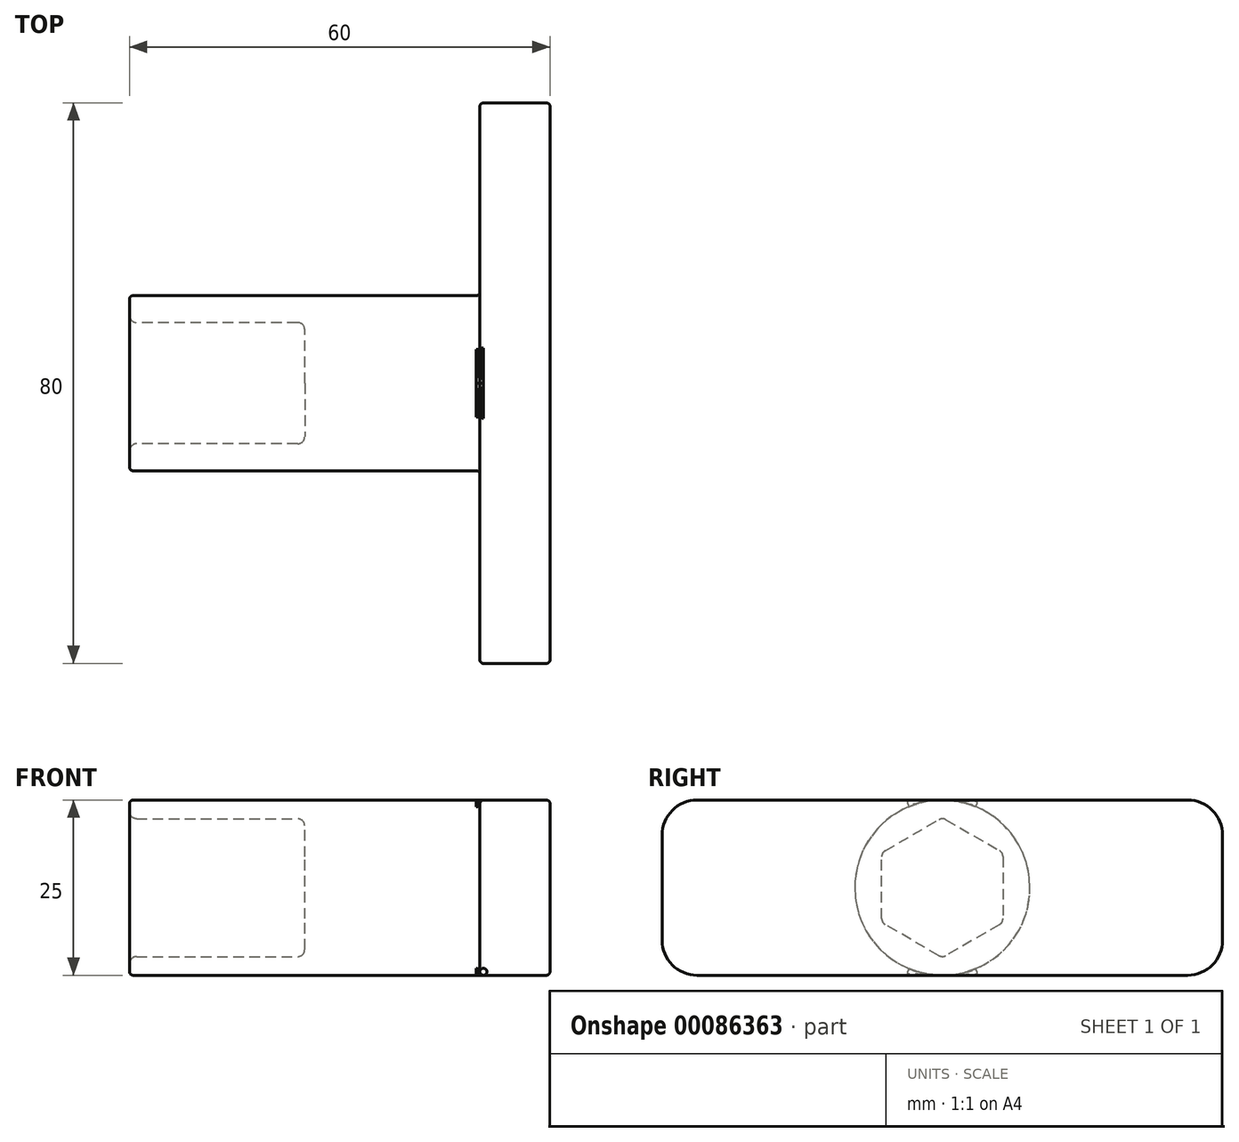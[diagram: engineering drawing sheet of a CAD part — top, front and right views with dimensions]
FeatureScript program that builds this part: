
annotation { "Feature Type Name" : "Feature", "Feature Type Description" : "" }
export const myFeature = defineFeature(function(context is Context, id is Id, definition is map)
    precondition{}
    {
        {
            var Q0;
            Q0=qCreatedBy(makeId("Right.planeOp"),FACE);
            var sketch = newSketch(context, id + "F0", { "sketchPlane" : qUnion([Q0])});
            skCircle(sketch, "E0", {"center": v(0, 0) * mm, "radius": 12.5 * mm});
            skCircle(sketch, "E1.cCircle", {"center": v(0, 0) * mm, "radius": 8.65 * mm, "construction": true});
            skLineSegment(sketch, "E1.0", {"start": v(-8.65, 5) * mm, "end": v(0, 9.99) * mm});
            skLineSegment(sketch, "E1.1", {"start": v(0, 9.99) * mm, "end": v(8.65, 5) * mm});
            skLineSegment(sketch, "E1.2", {"start": v(8.65, 5) * mm, "end": v(8.65, -5) * mm});
            skLineSegment(sketch, "E1.3", {"start": v(8.65, -5) * mm, "end": v(0, -9.99) * mm});
            skLineSegment(sketch, "E1.4", {"start": v(0, -9.99) * mm, "end": v(-8.65, -5) * mm});
            skLineSegment(sketch, "E1.5", {"start": v(-8.65, -5) * mm, "end": v(-8.65, 5) * mm});
            skPoint(sketch, "E1.0.midPoint", {"position": v(-4.32, 7.5) * mm});
            skSolve(sketch);
        }
        {
            var Q0;
            Q0 = qSketchRegion(id + "F0", true);
            extrude(context, id + "F1", {"entities" : qUnion([Q0]), "depth" : 25 * mm, "offsetDistance" : 25 * mm});
        }
        {
            var Q0;
            Q0=makeQuery(id+"F1.opExtrude","CAP_FACE",FACE,{"disambiguationData":[OSD([sQuery(id+"F0.wireOp",EDGE,"E0"),sQuery(id+"F0.wireOp",EDGE,"E1.0"),sQuery(id+"F0.wireOp",EDGE,"E1.1"),sQuery(id+"F0.wireOp",EDGE,"E1.2"),sQuery(id+"F0.wireOp",EDGE,"E1.3"),sQuery(id+"F0.wireOp",EDGE,"E1.4"),sQuery(id+"F0.wireOp",EDGE,"E1.5")])],"isStart":false});
            extrude(context, id + "F2", {"entities" : qUnion([Q0]), "operationType" : NewBodyOperationType.ADD, "depth" : 25 * mm, "offsetDistance" : 25 * mm});
        }
        {
            var Q0;
            Q0=makeQuery(id+"F2.opExtrude","CAP_FACE",FACE,{"disambiguationData":[OSD([sQuery(id+"F0.wireOp",EDGE,"E0"),sQuery(id+"F0.wireOp",EDGE,"E1.0"),sQuery(id+"F0.wireOp",EDGE,"E1.1"),sQuery(id+"F0.wireOp",EDGE,"E1.2"),sQuery(id+"F0.wireOp",EDGE,"E1.3"),sQuery(id+"F0.wireOp",EDGE,"E1.4"),sQuery(id+"F0.wireOp",EDGE,"E1.5")])],"isStart":false});
            var sketch = newSketch(context, id + "F3", { "sketchPlane" : qUnion([Q0])});
            skLineSegment(sketch, "E2", {"start": v(0, 9.99) * mm, "end": v(0, -9.99) * mm});
            skLineSegment(sketch, "E3.bottom", {"start": v(40, 12.5) * mm, "end": v(-40, 12.5) * mm});
            skLineSegment(sketch, "E3.top", {"start": v(40, -12.5) * mm, "end": v(-40, -12.5) * mm});
            skLineSegment(sketch, "E3.left", {"start": v(40, 12.5) * mm, "end": v(40, -12.5) * mm});
            skLineSegment(sketch, "E3.right", {"start": v(-40, 12.5) * mm, "end": v(-40, -12.5) * mm});
            skPoint(sketch, "E3.middle", {"position": v(0, 0) * mm});
            skSolve(sketch);
        }
        {
            var Q0;
            Q0 = qSketchRegion(id + "F3", true);
            extrude(context, id + "F4", {"entities" : qUnion([Q0]), "operationType" : NewBodyOperationType.ADD, "depth" : 10 * mm, "offsetDistance" : 25 * mm});
        }
        {
            var Q0;
            Q0=makeQuery(id+"F4.opExtrude","SWEPT_EDGE",EDGE,{"disambiguationData":[OSD([sQuery(id+"F3.wireOp",EDGE,"E3.bottom"),sQuery(id+"F3.wireOp",EDGE,"E3.right")])]});
            var Q1;
            Q1=makeQuery(id+"F4.opExtrude","SWEPT_EDGE",EDGE,{"disambiguationData":[OSD([sQuery(id+"F3.wireOp",EDGE,"E3.top"),sQuery(id+"F3.wireOp",EDGE,"E3.right")])]});
            var Q2;
            Q2=makeQuery(id+"F4.opExtrude","SWEPT_EDGE",EDGE,{"disambiguationData":[OSD([sQuery(id+"F3.wireOp",EDGE,"E3.bottom"),sQuery(id+"F3.wireOp",EDGE,"E3.left")])]});
            var Q3;
            Q3=makeQuery(id+"F4.opExtrude","SWEPT_EDGE",EDGE,{"disambiguationData":[OSD([sQuery(id+"F3.wireOp",EDGE,"E3.top"),sQuery(id+"F3.wireOp",EDGE,"E3.left")])]});
            fillet(context, id + "F5", {"entities" : qUnion([Q0, Q1, Q2, Q3]), "radius" : 5 * mm, "tangentPropagation" : true, "allowEdgeOverflow" : false});
        }
        {
            var Q0;
            Q0=makeQuery(id+"F4.opExtrude","CAP_FACE",FACE,{"disambiguationData":[OSD([sQuery(id+"F3.wireOp",EDGE,"E3.bottom"),sQuery(id+"F3.wireOp",EDGE,"E3.top"),sQuery(id+"F3.wireOp",EDGE,"E3.left"),sQuery(id+"F3.wireOp",EDGE,"E3.right")])],"isStart":false});
            var Q1;
            {var subQ0=sQuery(id+"F0.wireOp",EDGE,"E0");Q1=makeQuery(id+"F2.boolean.opBoolean","MERGE",FACE,{"derivedFrom":[makeQuery(id+"F1.opExtrude","SWEPT_FACE",FACE,{"disambiguationData":[OSD([subQ0])]}),makeQuery(id+"F2.opExtrude","SWEPT_FACE",FACE,{"disambiguationData":[OSD([subQ0])]})]});}
            var Q2;
            {var subQ0=sQuery(id+"F3.wireOp",EDGE,"E3.right");var subQ1=sQuery(id+"F3.wireOp",EDGE,"E3.top");var subQ2=sQuery(id+"F3.wireOp",EDGE,"E3.bottom");var subQ3=makeQuery(id+"F4.opExtrude","CAP_FACE",FACE,{"disambiguationData":[OSD([subQ2,subQ1,sQuery(id+"F3.wireOp",EDGE,"E3.left"),subQ0])],"isStart":true});Q2=makeQuery(id+"F5.opFillet","BLEND_EDGE",EDGE,{"blendedFrom":[makeQuery(id+"F4.opExtrude","SWEPT_EDGE",EDGE,{"disambiguationData":[OSD([subQ1,subQ0])]}),makeQuery(id+"F4.boolean.opBoolean","SPLIT",FACE,{"disambiguationData":[TD([makeQuery(id+"F4.opExtrude","SWEPT_FACE",FACE,{"disambiguationData":[OSD([subQ0])]})])],"derivedFrom":subQ3})],"blendedInto":[makeQuery(id+"F4.boolean.opBoolean","SPLIT",FACE,{"disambiguationData":[TD([makeQuery(id+"F4.opExtrude","SWEPT_FACE",FACE,{"disambiguationData":[OSD([subQ0])]})])],"derivedFrom":subQ3})]});}
            var Q3;
            {var subQ0=sQuery(id+"F3.wireOp",EDGE,"E3.top");var subQ1=sQuery(id+"F3.wireOp",EDGE,"E3.left");Q3=makeQuery(id+"F4.boolean.opBoolean","SPLIT",EDGE,{"disambiguationData":[TD([makeQuery(id+"F4.opExtrude","SWEPT_FACE",FACE,{"disambiguationData":[OSD([subQ1])]})])],"derivedFrom":makeQuery(id+"F4.opExtrude","CAP_EDGE",EDGE,{"disambiguationData":[OSD([subQ0])],"isStart":true})});}
            fillet(context, id + "F6", {"entities" : qUnion([Q0, Q1, Q2, Q3]), "radius" : .5 * mm, "tangentPropagation" : true, "allowEdgeOverflow" : false});
        }
        {
            var Q0;
            {var subQ4=sQuery(id+"F0.wireOp",EDGE,"E1.0");Q0=makeQuery(id+"F4.boolean.opBoolean","SPLIT",FACE,{"disambiguationData":[TD([makeQuery(id+"F1.opExtrude","SWEPT_FACE",FACE,{"disambiguationData":[OSD([subQ4])]})])],"derivedFrom":makeQuery(id+"F4.opExtrude","CAP_FACE",FACE,{"disambiguationData":[OSD([sQuery(id+"F3.wireOp",EDGE,"E3.bottom"),sQuery(id+"F3.wireOp",EDGE,"E3.top"),sQuery(id+"F3.wireOp",EDGE,"E3.left"),sQuery(id+"F3.wireOp",EDGE,"E3.right")])],"isStart":true})});}
            extrude(context, id + "F7", {"entities" : qUnion([Q0]), "operationType" : NewBodyOperationType.ADD, "depth" : 25 * mm, "offsetDistance" : 25 * mm});
        }
        {
            var Q0;
            {var subQ0=sQuery(id+"F0.wireOp",EDGE,"E1.4");var subQ1=sQuery(id+"F0.wireOp",EDGE,"E1.3");Q0=makeQuery(id+"F2.boolean.opBoolean","MERGE",EDGE,{"derivedFrom":[makeQuery(id+"F1.opExtrude","SWEPT_EDGE",EDGE,{"disambiguationData":[OSD([subQ1,subQ0])]}),makeQuery(id+"F2.opExtrude","SWEPT_EDGE",EDGE,{"disambiguationData":[OSD([subQ1,subQ0])]})]});}
            var Q1;
            {var subQ0=sQuery(id+"F0.wireOp",EDGE,"E1.3");var subQ1=sQuery(id+"F0.wireOp",EDGE,"E1.2");Q1=makeQuery(id+"F2.boolean.opBoolean","MERGE",EDGE,{"derivedFrom":[makeQuery(id+"F1.opExtrude","SWEPT_EDGE",EDGE,{"disambiguationData":[OSD([subQ1,subQ0])]}),makeQuery(id+"F2.opExtrude","SWEPT_EDGE",EDGE,{"disambiguationData":[OSD([subQ1,subQ0])]})]});}
            var Q2;
            {var subQ0=sQuery(id+"F0.wireOp",EDGE,"E1.5");var subQ1=sQuery(id+"F0.wireOp",EDGE,"E1.4");Q2=makeQuery(id+"F2.boolean.opBoolean","MERGE",EDGE,{"derivedFrom":[makeQuery(id+"F1.opExtrude","SWEPT_EDGE",EDGE,{"disambiguationData":[OSD([subQ1,subQ0])]}),makeQuery(id+"F2.opExtrude","SWEPT_EDGE",EDGE,{"disambiguationData":[OSD([subQ1,subQ0])]})]});}
            var Q3;
            {var subQ0=sQuery(id+"F0.wireOp",EDGE,"E1.5");var subQ1=sQuery(id+"F0.wireOp",EDGE,"E1.0");Q3=makeQuery(id+"F2.boolean.opBoolean","MERGE",EDGE,{"derivedFrom":[makeQuery(id+"F1.opExtrude","SWEPT_EDGE",EDGE,{"disambiguationData":[OSD([subQ1,subQ0])]}),makeQuery(id+"F2.opExtrude","SWEPT_EDGE",EDGE,{"disambiguationData":[OSD([subQ1,subQ0])]})]});}
            var Q4;
            {var subQ0=sQuery(id+"F0.wireOp",EDGE,"E1.1");var subQ1=sQuery(id+"F0.wireOp",EDGE,"E1.0");Q4=makeQuery(id+"F2.boolean.opBoolean","MERGE",EDGE,{"derivedFrom":[makeQuery(id+"F1.opExtrude","SWEPT_EDGE",EDGE,{"disambiguationData":[OSD([subQ1,subQ0])]}),makeQuery(id+"F2.opExtrude","SWEPT_EDGE",EDGE,{"disambiguationData":[OSD([subQ1,subQ0])]})]});}
            var Q5;
            {var subQ0=sQuery(id+"F0.wireOp",EDGE,"E1.2");var subQ1=sQuery(id+"F0.wireOp",EDGE,"E1.1");Q5=makeQuery(id+"F2.boolean.opBoolean","MERGE",EDGE,{"derivedFrom":[makeQuery(id+"F1.opExtrude","SWEPT_EDGE",EDGE,{"disambiguationData":[OSD([subQ1,subQ0])]}),makeQuery(id+"F2.opExtrude","SWEPT_EDGE",EDGE,{"disambiguationData":[OSD([subQ1,subQ0])]})]});}
            fillet(context, id + "F8", {"entities" : qUnion([Q0, Q1, Q2, Q3, Q4, Q5]), "radius" : 1 * mm, "tangentPropagation" : true, "allowEdgeOverflow" : false});
        }
        {
            var Q0;
            Q0=makeQuery(id+"F7.opExtrude","CAP_FACE",FACE,{"disambiguationData":[OSD([sQuery(id+"F3.wireOp",EDGE,"E3.bottom"),sQuery(id+"F3.wireOp",EDGE,"E3.top"),sQuery(id+"F3.wireOp",EDGE,"E3.left"),sQuery(id+"F3.wireOp",EDGE,"E3.right")])],"isStart":false});
            var Q1;
            Q1=makeQuery(id+"F1.opExtrude","CAP_EDGE",EDGE,{"disambiguationData":[OSD([sQuery(id+"F0.wireOp",EDGE,"E1.4")])],"isStart":true});
            fillet(context, id + "F9", {"entities" : qUnion([Q0, Q1]), "radius" : 1 * mm, "tangentPropagation" : true, "allowEdgeOverflow" : false});
        }
    });
